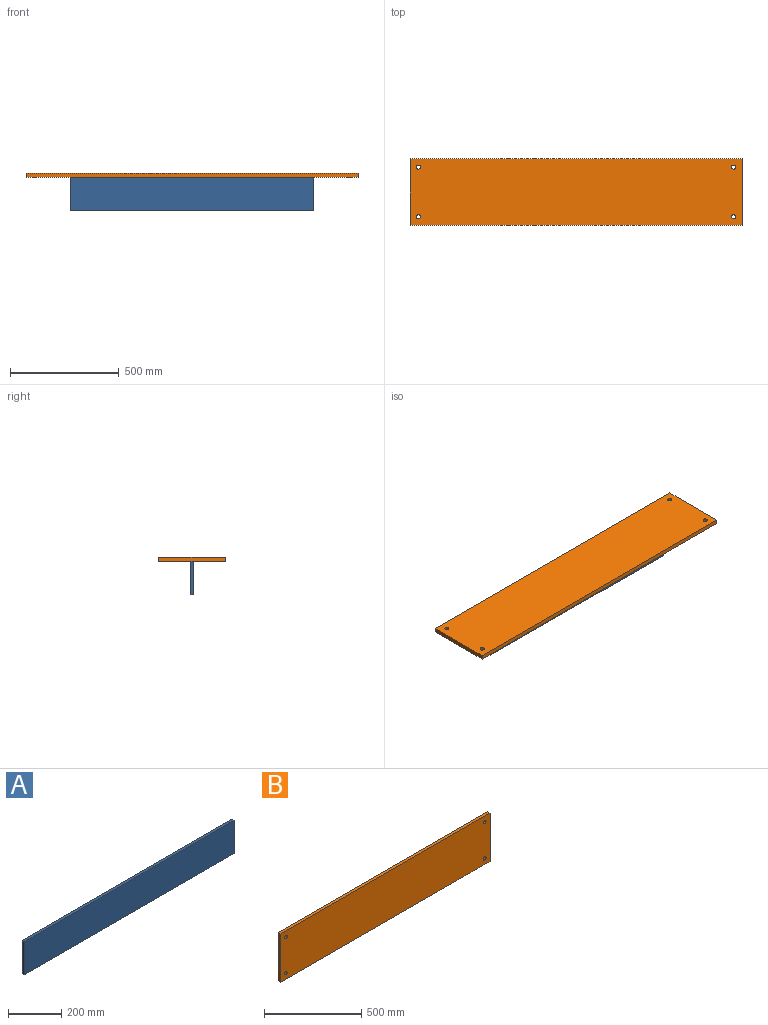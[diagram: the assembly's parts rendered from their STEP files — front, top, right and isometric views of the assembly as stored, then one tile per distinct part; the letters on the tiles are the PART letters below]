
ASSEMBLY  parts=2 mates=1
PART A: 6 faces, bbox 1117.6x12.7x152.4 mm
  f0: plane 1117.6x12.7mm, normal (0,0,1), area 14193.5mm2, adj f1,f3,f4,f5
  f1: plane 152.4x12.7mm, normal (-1,0,0), area 1935.5mm2, adj f0,f2,f4,f5
  f2: plane 1117.6x12.7mm, normal (0,0,-1), area 14193.5mm2, adj f1,f3,f4,f5
  f3: plane 152.4x12.7mm, normal (1,0,0), area 1935.5mm2, adj f0,f2,f4,f5
  f4: plane 1117.6x152.4mm, normal (0,-1,0), area 170322.2mm2, adj f0,f1,f2,f3
  f5: plane 1117.6x152.4mm, normal (0,1,0), area 170322.2mm2, adj f0,f1,f2,f3
PART B: 10 faces, bbox 1524x19.1x304.8 mm
  f0: plane 1524x19.05mm, normal (0,0,1), area 29032.2mm2, adj f1,f7,f8,f9
  f1: plane 304.8x19.05mm, normal (-1,0,0), area 5806.4mm2, adj f0,f2,f8,f9
  f2: plane 1524x19.05mm, normal (0,0,-1), area 29032.2mm2, adj f1,f7,f8,f9
  f3: cylinder r=9.53mm len=19.05mm, axis (0,1,0), area 1140.1mm2, adj f8,f9
  f4: cylinder r=9.53mm len=19.05mm, axis (0,1,0), area 1140.1mm2, adj f8,f9
  f5: cylinder r=9.53mm len=19.05mm, axis (0,1,0), area 1140.1mm2, adj f8,f9
  f6: cylinder r=9.53mm len=19.05mm, axis (0,1,0), area 1140.1mm2, adj f8,f9
  f7: plane 304.8x19.05mm, normal (1,0,0), area 5806.4mm2, adj f0,f2,f8,f9
  f8: plane 1524x304.8mm, normal (0,-1,0), area 463375.1mm2, adj f0,f1,f2,f3,f4,f5,f6,f7
  f9: plane 1524x304.8mm, normal (0,1,0), area 463375.1mm2, adj f0,f1,f2,f3,f4,f5,f6,f7
PLACE A t=(31.63,176.14,227.29)mm
PLACE B rot(axis=(1,0,0),90deg) t=(31.63,169.79,322.54)mm
MATE fastened B.f8 <-> A.f0  axis (0,0,-1) through (31.63,169.79,303.49)mm
